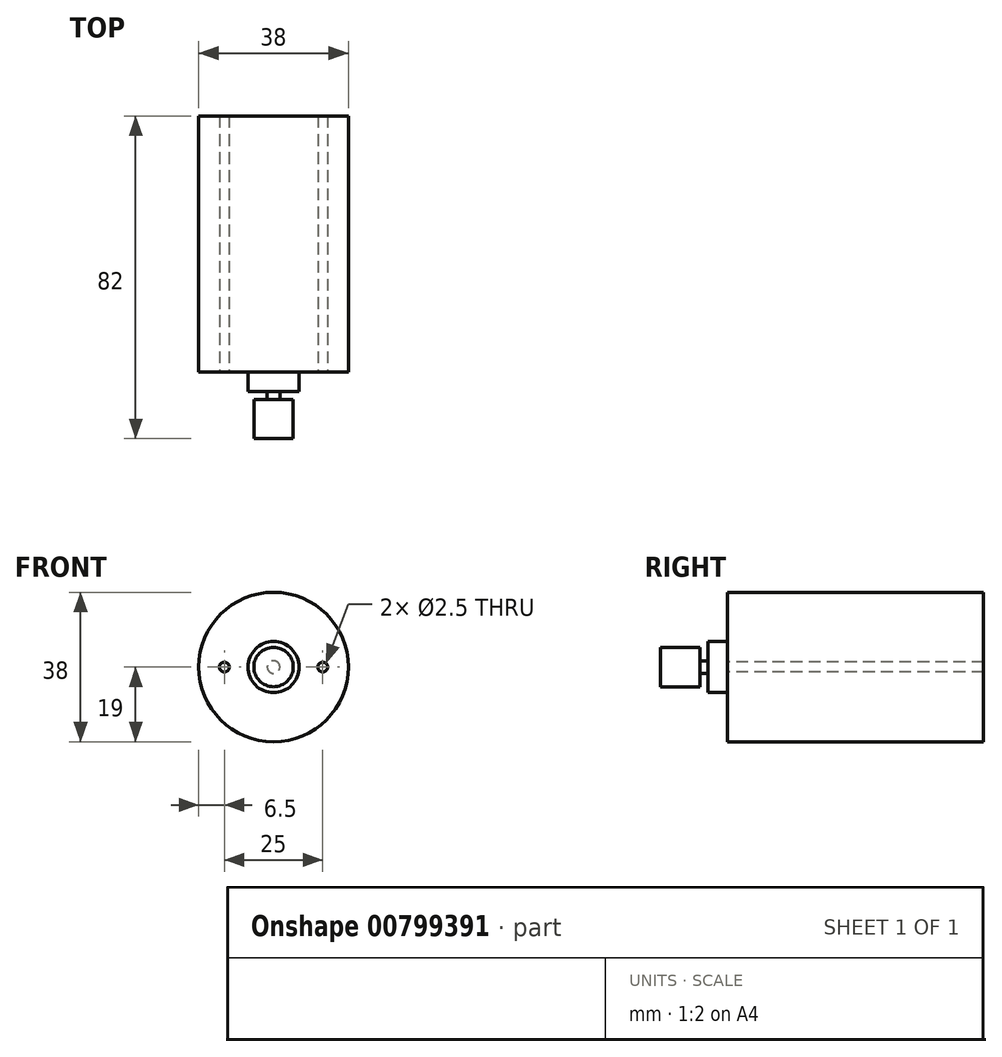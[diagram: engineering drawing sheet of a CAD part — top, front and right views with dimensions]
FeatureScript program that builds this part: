
annotation { "Feature Type Name" : "Feature", "Feature Type Description" : "" }
export const myFeature = defineFeature(function(context is Context, id is Id, definition is map)
    precondition{}
    {
        {
            var Q0;
            Q0=qCreatedBy(makeId("Front.planeOp"),FACE);
            var sketch = newSketch(context, id + "F0", { "sketchPlane" : qUnion([Q0])});
            skCircle(sketch, "E0", {"center": v(0, 0) * mm, "radius": 19 * mm});
            skCircle(sketch, "E1", {"center": v(0, 0) * mm, "radius": 6.5 * mm});
            skCircle(sketch, "E2", {"center": v(-12.5, 0) * mm, "radius": 1.25 * mm});
            skCircle(sketch, "E3.MirrorC", {"center": v(12.5, 0) * mm, "radius": 1.25 * mm});
            skSolve(sketch);
        }
        {
            var Q0;
            Q0=makeQuery(id+"F0.imprint","IMPRINT",FACE,{"disambiguationData":[TD([[makeQuery(id+"F0.imprint","IMPRINT",EDGE,{"derivedFrom":sQuery(id+"F0.wireOp",EDGE,"E0")}),1.0]])]});
            var Q1;
            Q1=makeQuery(id+"F0.imprint","IMPRINT",FACE,{"disambiguationData":[TD([[makeQuery(id+"F0.imprint","IMPRINT",EDGE,{"derivedFrom":sQuery(id+"F0.wireOp",EDGE,"E1")}),1.0]])]});
            extrude(context, id + "F1", {"entities" : qUnion([Q0, Q1]), "oppositeDirection" : true, "depth" : 65 * mm, "offsetDistance" : 25 * mm});
        }
        {
            var Q0;
            Q0=makeQuery(id+"F0.imprint","IMPRINT",FACE,{"disambiguationData":[TD([[makeQuery(id+"F0.imprint","IMPRINT",EDGE,{"derivedFrom":sQuery(id+"F0.wireOp",EDGE,"E1")}),1.0]])]});
            extrude(context, id + "F2", {"entities" : qUnion([Q0]), "operationType" : NewBodyOperationType.ADD, "depth" : 5 * mm, "offsetDistance" : 25 * mm});
        }
        {
            var Q0;
            Q0=makeQuery(id+"F2.opExtrude","CAP_FACE",FACE,{"disambiguationData":[OSD([sQuery(id+"F0.wireOp",EDGE,"E1")])],"isStart":false});
            var sketch = newSketch(context, id + "F3", { "sketchPlane" : qUnion([Q0])});
            skCircle(sketch, "E4", {"center": v(0, 0) * mm, "radius": 1.6 * mm});
            skSolve(sketch);
        }
        {
            var Q0;
            Q0=makeQuery(id+"F3.imprint","IMPRINT",FACE,{"disambiguationData":[TD([[makeQuery(id+"F3.imprint","IMPRINT",EDGE,{"derivedFrom":sQuery(id+"F3.wireOp",EDGE,"E4")}),1.0]])]});
            extrude(context, id + "F4", {"entities" : qUnion([Q0]), "operationType" : NewBodyOperationType.ADD, "depth" : 12 * mm, "offsetDistance" : 25 * mm});
        }
        {
            var Q0;
            Q0=makeQuery(id+"F4.opExtrude","CAP_FACE",FACE,{"disambiguationData":[OSD([sQuery(id+"F3.wireOp",EDGE,"E4")])],"isStart":false});
            var sketch = newSketch(context, id + "F5", { "sketchPlane" : qUnion([Q0])});
            skCircle(sketch, "E5", {"center": v(0, 0) * mm, "radius": 5 * mm});
            skCircle(sketch, "E6.0", {"center": v(0, 0) * mm, "radius": 1.6 * mm});
            skSolve(sketch);
        }
        {
            var Q0;
            Q0=makeQuery(id+"F5.imprint","IMPRINT",FACE,{"disambiguationData":[TD([[makeQuery(id+"F5.imprint","IMPRINT",EDGE,{"derivedFrom":sQuery(id+"F5.wireOp",EDGE,"E5")}),1.0]])]});
            extrude(context, id + "F6", {"entities" : qUnion([Q0]), "operationType" : NewBodyOperationType.ADD, "oppositeDirection" : true, "depth" : 10 * mm, "offsetDistance" : 25 * mm});
        }
    });
